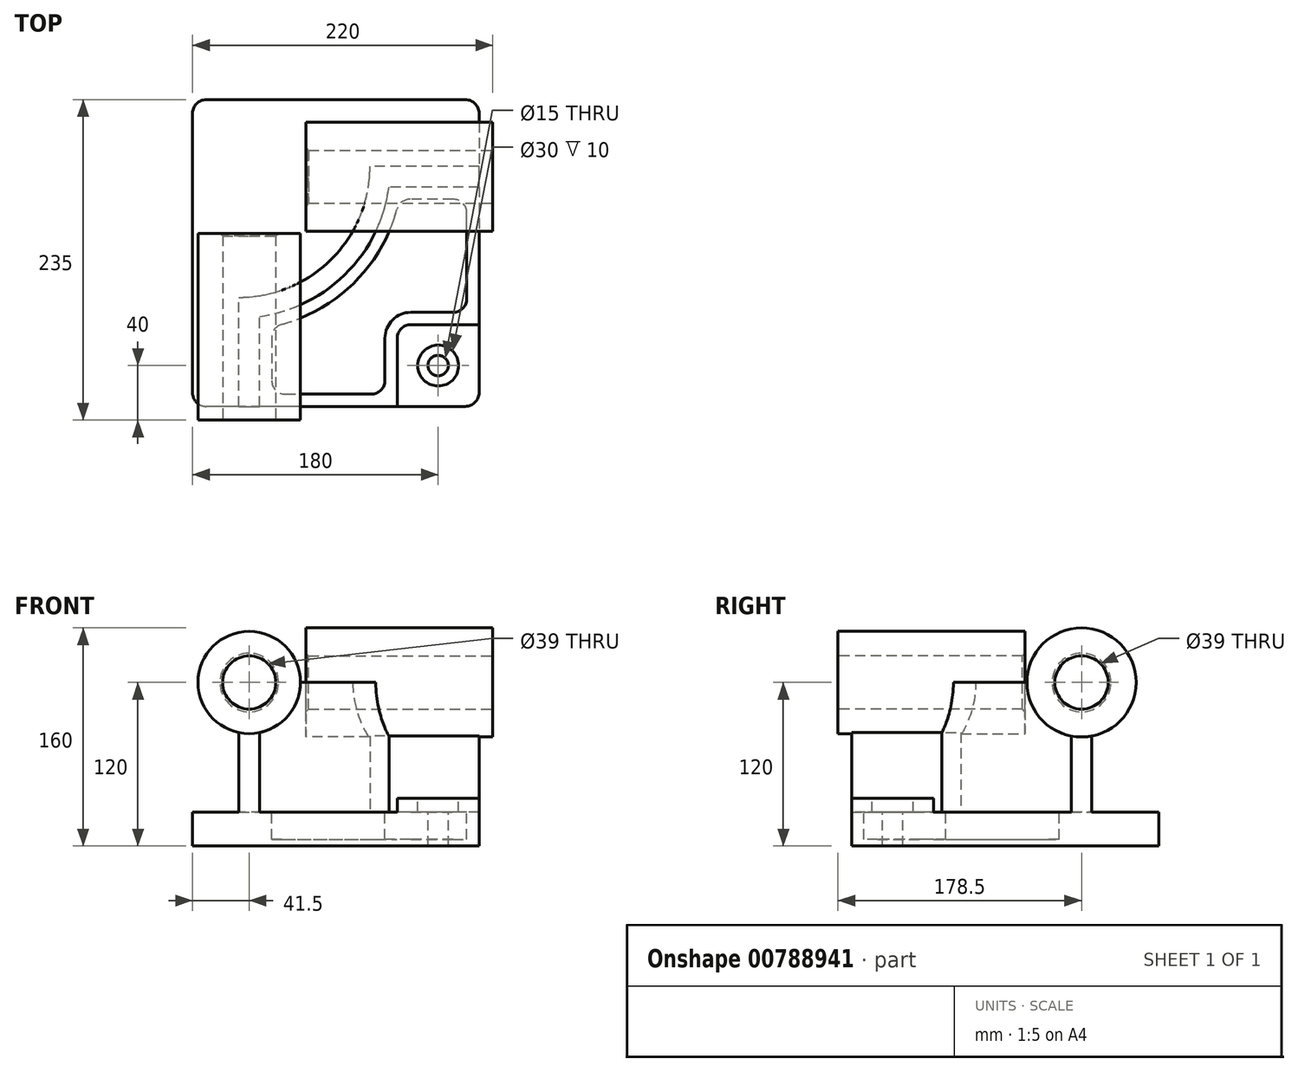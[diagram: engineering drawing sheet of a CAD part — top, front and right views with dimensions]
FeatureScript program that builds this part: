
annotation { "Feature Type Name" : "Feature", "Feature Type Description" : "" }
export const myFeature = defineFeature(function(context is Context, id is Id, definition is map)
    precondition{}
    {
        {
            var Q0;
            Q0=qCreatedBy(makeId("Top.planeOp"),FACE);
            var sketch = newSketch(context, id + "F0", { "sketchPlane" : qUnion([Q0])});
            skLineSegment(sketch, "E0.bottom", {"start": v(105, 112.5) * mm, "end": v(-105, 112.5) * mm});
            skLineSegment(sketch, "E0.top", {"start": v(105, -112.5) * mm, "end": v(-105, -112.5) * mm});
            skLineSegment(sketch, "E0.left", {"start": v(105, 112.5) * mm, "end": v(105, -112.5) * mm});
            skLineSegment(sketch, "E0.right", {"start": v(-105, 112.5) * mm, "end": v(-105, -112.5) * mm});
            skPoint(sketch, "E0.middle", {"position": v(0, 0) * mm});
            skSolve(sketch);
        }
        {
            var Q0;
            Q0=makeQuery(id+"F0.imprint","IMPRINT",FACE,{"disambiguationData":[TD([[makeQuery(id+"F0.imprint","IMPRINT",EDGE,{"derivedFrom":sQuery(id+"F0.wireOp",EDGE,"E0.bottom")}),1.0]])]});
            extrude(context, id + "F1", {"entities" : qUnion([Q0]), "depth" : 25 * mm, "offsetDistance" : 25 * mm});
        }
        {
            var Q0;
            Q0=makeQuery(id+"F1.opExtrude","CAP_FACE",FACE,{"disambiguationData":[OSD([sQuery(id+"F0.wireOp",EDGE,"E0.bottom"),sQuery(id+"F0.wireOp",EDGE,"E0.top"),sQuery(id+"F0.wireOp",EDGE,"E0.left"),sQuery(id+"F0.wireOp",EDGE,"E0.right")])],"isStart":false});
            var sketch = newSketch(context, id + "F2", { "sketchPlane" : qUnion([Q0])});
            skLineSegment(sketch, "E1", {"start": v(-71, -112.5) * mm, "end": v(-71, -32.5) * mm});
            skLineSegment(sketch, "E2", {"start": v(105, 63.5) * mm, "end": v(25, 63.5) * mm});
            skArc(sketch, "E3", {"start": v(-71, -32.5) * mm, "mid": v(-3.12, -4.38) * mm, "end": v(25, 63.5) * mm});
            skLineSegment(sketch, "E4", {"start": v(-71, 63.5) * mm, "end": v(-71, -32.5) * mm, "construction": true});
            skLineSegment(sketch, "E5", {"start": v(25, 63.5) * mm, "end": v(-71, 63.5) * mm, "construction": true});
            skLineSegment(sketch, "E6.0", {"start": v(-56, -112.5) * mm, "end": v(-56, -46.48) * mm});
            skArc(sketch, "E6.1", {"start": v(-56, -46.48) * mm, "mid": v(7.49, -14.99) * mm, "end": v(38.98, 48.5) * mm});
            skLineSegment(sketch, "E6.2", {"start": v(105, 48.5) * mm, "end": v(38.98, 48.5) * mm});
            skLineSegment(sketch, "E7.0", {"start": v(105, 112.5) * mm, "end": v(105, -112.5) * mm});
            skLineSegment(sketch, "E8.0.0", {"start": v(-105, -112.5) * mm, "end": v(105, -112.5) * mm});
            skLineSegment(sketch, "E8.0.1", {"start": v(105, -112.5) * mm, "end": v(105, 112.5) * mm});
            skLineSegment(sketch, "E8.0.2", {"start": v(105, 112.5) * mm, "end": v(-105, 112.5) * mm});
            skLineSegment(sketch, "E8.0.3", {"start": v(-105, 112.5) * mm, "end": v(-105, -112.5) * mm});
            skSolve(sketch);
        }
        {
            var Q0;
            {var subQ2=sQuery(id+"F2.wireOp",EDGE,"E1");Q0=makeQuery(id+"F2.imprint","IMPRINT",FACE,{"disambiguationData":[TD([[makeQuery(id+"F2.imprint","IMPRINT",EDGE,{"derivedFrom":subQ2}),-1.0]])]});}
            extrude(context, id + "F3", {"entities" : qUnion([Q0]), "operationType" : NewBodyOperationType.ADD, "depth" : 95 * mm, "offsetDistance" : 25 * mm});
        }
        {
            var Q0;
            Q0=makeQuery(id+"F3.boolean.opBoolean","MERGE",FACE,{"derivedFrom":[makeQuery(id+"F1.opExtrude","SWEPT_FACE",FACE,{"disambiguationData":[OSD([sQuery(id+"F0.wireOp",EDGE,"E0.top")])]}),makeQuery(id+"F3.opExtrude","SWEPT_FACE",FACE,{"disambiguationData":[OSD([sQuery(id+"F2.wireOp",EDGE,"E8.0.0")])]})]});
            var sketch = newSketch(context, id + "F4", { "sketchPlane" : qUnion([Q0])});
            skCircle(sketch, "E9", {"center": v(-63.5, 120) * mm, "radius": 37.5 * mm});
            skSolve(sketch);
        }
        {
            var Q0;
            Q0 = qSketchRegion(id + "F4", true);
            extrude(context, id + "F5", {"entities" : qUnion([Q0]), "operationType" : NewBodyOperationType.ADD, "depth" : 10 * mm, "offsetDistance" : 25 * mm, "hasSecondDirection" : true, "secondDirectionOppositeDirection" : true, "secondDirectionDepth" : 127 * mm});
        }
        {
            var Q0;
            Q0=makeQuery(id+"F3.boolean.opBoolean","MERGE",FACE,{"derivedFrom":[makeQuery(id+"F1.opExtrude","SWEPT_FACE",FACE,{"disambiguationData":[OSD([sQuery(id+"F0.wireOp",EDGE,"E0.left")])]}),makeQuery(id+"F3.opExtrude","SWEPT_FACE",FACE,{"disambiguationData":[OSD([sQuery(id+"F2.wireOp",EDGE,"E8.0.1")])]})]});
            var sketch = newSketch(context, id + "F6", { "sketchPlane" : qUnion([Q0])});
            skCircle(sketch, "E10", {"center": v(56, 120) * mm, "radius": 40 * mm});
            skSolve(sketch);
        }
        {
            var Q0;
            Q0 = qSketchRegion(id + "F6", true);
            extrude(context, id + "F7", {"entities" : qUnion([Q0]), "operationType" : NewBodyOperationType.ADD, "depth" : 10 * mm, "offsetDistance" : 25 * mm, "hasSecondDirection" : true, "secondDirectionOppositeDirection" : true, "secondDirectionDepth" : 127 * mm});
        }
        {
            var Q0;
            {var subQ0=sQuery(id+"F0.wireOp",EDGE,"E0.left");var subQ1=sQuery(id+"F0.wireOp",EDGE,"E0.top");Q0=makeQuery(id+"F3.boolean.opBoolean","SPLIT",FACE,{"disambiguationData":[TD([makeQuery(id+"F3.opExtrude","SWEPT_FACE",FACE,{"disambiguationData":[OSD([sQuery(id+"F2.wireOp",EDGE,"E6.0")])]})])],"derivedFrom":makeQuery(id+"F1.opExtrude","CAP_FACE",FACE,{"disambiguationData":[OSD([sQuery(id+"F0.wireOp",EDGE,"E0.bottom"),subQ1,subQ0,sQuery(id+"F0.wireOp",EDGE,"E0.right")])],"isStart":false})});}
            var sketch = newSketch(context, id + "F8", { "sketchPlane" : qUnion([Q0])});
            skLineSegment(sketch, "E11.bottom", {"start": v(105, -112.5) * mm, "end": v(45, -112.5) * mm});
            skLineSegment(sketch, "E11.top", {"start": v(105, -52.5) * mm, "end": v(45, -52.5) * mm});
            skLineSegment(sketch, "E11.left", {"start": v(105, -112.5) * mm, "end": v(105, -52.5) * mm});
            skLineSegment(sketch, "E11.right", {"start": v(45, -112.5) * mm, "end": v(45, -52.5) * mm});
            skSolve(sketch);
        }
        {
            var Q0;
            Q0 = qSketchRegion(id + "F8", true);
            extrude(context, id + "F9", {"entities" : qUnion([Q0]), "operationType" : NewBodyOperationType.ADD, "depth" : 10 * mm, "offsetDistance" : 25 * mm});
        }
        {
            var Q0;
            Q0=makeQuery(id+"F9.opExtrude","SWEPT_EDGE",EDGE,{"disambiguationData":[OSD([sQuery(id+"F8.wireOp",EDGE,"E11.top"),sQuery(id+"F8.wireOp",EDGE,"E11.right")])]});
            fillet(context, id + "F10", {"entities" : qUnion([Q0]), "radius" : 10 * mm, "tangentPropagation" : true, "allowEdgeOverflow" : false});
        }
        {
            var Q0;
            {var subQ0=sQuery(id+"F0.wireOp",EDGE,"E0.left");var subQ1=sQuery(id+"F0.wireOp",EDGE,"E0.top");Q0=makeQuery(id+"F3.boolean.opBoolean","SPLIT",FACE,{"disambiguationData":[TD([makeQuery(id+"F3.opExtrude","SWEPT_FACE",FACE,{"disambiguationData":[OSD([sQuery(id+"F2.wireOp",EDGE,"E6.0")])]})])],"derivedFrom":makeQuery(id+"F1.opExtrude","CAP_FACE",FACE,{"disambiguationData":[OSD([sQuery(id+"F0.wireOp",EDGE,"E0.bottom"),subQ1,subQ0,sQuery(id+"F0.wireOp",EDGE,"E0.right")])],"isStart":false})});}
            var sketch = newSketch(context, id + "F11", { "sketchPlane" : qUnion([Q0])});
            skLineSegment(sketch, "E12.0", {"start": v(-47, -54.08) * mm, "end": v(-47, -103.5) * mm});
            skArc(sketch, "E12.1", {"start": v(46.58, 39.5) * mm, "mid": v(13.85, -21.35) * mm, "end": v(-47, -54.08) * mm});
            skLineSegment(sketch, "E12.2", {"start": v(-47, -103.5) * mm, "end": v(36, -103.5) * mm});
            skLineSegment(sketch, "E12.3", {"start": v(96, 39.5) * mm, "end": v(46.58, 39.5) * mm});
            skLineSegment(sketch, "E12.4", {"start": v(36, -103.5) * mm, "end": v(36, -62.5) * mm});
            skArc(sketch, "E12.5", {"start": v(36, -62.5) * mm, "mid": v(41.56, -49.06) * mm, "end": v(55, -43.5) * mm});
            skLineSegment(sketch, "E12.6", {"start": v(55, -43.5) * mm, "end": v(96, -43.5) * mm});
            skLineSegment(sketch, "E12.7", {"start": v(96, -43.5) * mm, "end": v(96, 39.5) * mm});
            skSolve(sketch);
        }
        {
            var Q0;
            Q0=makeQuery(id+"F11.imprint","IMPRINT",FACE,{"disambiguationData":[TD([[makeQuery(id+"F11.imprint","IMPRINT",EDGE,{"derivedFrom":sQuery(id+"F11.wireOp",EDGE,"E12.0")}),1.0]])]});
            extrude(context, id + "F12", {"entities" : qUnion([Q0]), "operationType" : NewBodyOperationType.REMOVE, "oppositeDirection" : true, "depth" : 20 * mm, "offsetDistance" : 25 * mm});
        }
        {
            var Q0;
            Q0=makeQuery(id+"F9.opExtrude","CAP_FACE",FACE,{"disambiguationData":[OSD([sQuery(id+"F8.wireOp",EDGE,"E11.bottom"),sQuery(id+"F8.wireOp",EDGE,"E11.top"),sQuery(id+"F8.wireOp",EDGE,"E11.left"),sQuery(id+"F8.wireOp",EDGE,"E11.right")])],"isStart":false});
            var sketch = newSketch(context, id + "F13", { "sketchPlane" : qUnion([Q0])});
            skCircle(sketch, "E13", {"center": v(75, -82.5) * mm, "radius": 15 * mm});
            skSolve(sketch);
        }
        {
            var Q0;
            Q0=sQuery(id+"F13.wireOp",VERTEX,"E13.center");
            var Q1;
            Q1=makeQuery(id+"F1.opExtrude","SWEPT_BODY",BODY,{"disambiguationData":[OSD([sQuery(id+"F0.wireOp",EDGE,"E0.bottom"),sQuery(id+"F0.wireOp",EDGE,"E0.top"),sQuery(id+"F0.wireOp",EDGE,"E0.left"),sQuery(id+"F0.wireOp",EDGE,"E0.right")])]});
            hole(context, id + "F14", {"style" : HoleStyle.C_BORE, "endStyle" : HoleEndStyle.THROUGH, "holeDiameter" : 15 * mm, "cBoreDiameter" : 30 * mm, "cBoreDepth" : 10 * mm, "majorDiameter" : 6.35 * mm, "isTappedThrough" : true, "tappedDepth" : 12 * mm, "tapClearance" : 3, "locations" : qUnion([Q0]), "scope" : qUnion([Q1])});
        }
        {
            var Q0;
            Q0=makeQuery(id+"F12.boolean.opBoolean","COPY",EDGE,{"derivedFrom":makeQuery(id+"F12.opExtrude","SWEPT_EDGE",EDGE,{"disambiguationData":[OSD([sQuery(id+"F11.wireOp",EDGE,"E12.0"),sQuery(id+"F11.wireOp",EDGE,"E12.1")])]})});
            var Q1;
            Q1=makeQuery(id+"F12.boolean.opBoolean","COPY",EDGE,{"derivedFrom":makeQuery(id+"F12.opExtrude","SWEPT_EDGE",EDGE,{"disambiguationData":[OSD([sQuery(id+"F11.wireOp",EDGE,"E12.1"),sQuery(id+"F11.wireOp",EDGE,"E12.3")])]})});
            var Q2;
            Q2=makeQuery(id+"F12.boolean.opBoolean","COPY",EDGE,{"derivedFrom":makeQuery(id+"F12.opExtrude","SWEPT_EDGE",EDGE,{"disambiguationData":[OSD([sQuery(id+"F11.wireOp",EDGE,"E12.2"),sQuery(id+"F11.wireOp",EDGE,"E12.4")])]})});
            var Q3;
            Q3=makeQuery(id+"F12.boolean.opBoolean","COPY",EDGE,{"derivedFrom":makeQuery(id+"F12.opExtrude","SWEPT_EDGE",EDGE,{"disambiguationData":[OSD([sQuery(id+"F11.wireOp",EDGE,"E12.6"),sQuery(id+"F11.wireOp",EDGE,"E12.7")])]})});
            var Q4;
            Q4=makeQuery(id+"F12.boolean.opBoolean","COPY",EDGE,{"derivedFrom":makeQuery(id+"F12.opExtrude","SWEPT_EDGE",EDGE,{"disambiguationData":[OSD([sQuery(id+"F11.wireOp",EDGE,"E12.3"),sQuery(id+"F11.wireOp",EDGE,"E12.7")])]})});
            var Q5;
            Q5=makeQuery(id+"F12.boolean.opBoolean","COPY",EDGE,{"derivedFrom":makeQuery(id+"F12.opExtrude","SWEPT_EDGE",EDGE,{"disambiguationData":[OSD([sQuery(id+"F11.wireOp",EDGE,"E12.0"),sQuery(id+"F11.wireOp",EDGE,"E12.2")])]})});
            fillet(context, id + "F15", {"entities" : qUnion([Q0, Q1, Q2, Q3, Q4, Q5]), "radius" : 10 * mm, "tangentPropagation" : true, "allowEdgeOverflow" : false});
        }
        {
            var Q0;
            Q0=makeQuery(id+"F5.opExtrude","CAP_FACE",FACE,{"disambiguationData":[OSD([sQuery(id+"F4.wireOp",EDGE,"E9")])],"isStart":false});
            var sketch = newSketch(context, id + "F16", { "sketchPlane" : qUnion([Q0])});
            skCircle(sketch, "E14", {"center": v(-63.5, 120) * mm, "radius": 19.5 * mm});
            skSolve(sketch);
        }
        {
            var Q0;
            Q0 = qSketchRegion(id + "F16", true);
            extrude(context, id + "F17", {"entities" : qUnion([Q0]), "operationType" : NewBodyOperationType.REMOVE, "endBound" : BoundingType.THROUGH_ALL, "oppositeDirection" : true, "depth" : 25 * mm, "offsetDistance" : 25 * mm});
        }
        {
            var Q0;
            Q0=makeQuery(id+"F7.opExtrude","CAP_FACE",FACE,{"disambiguationData":[OSD([sQuery(id+"F6.wireOp",EDGE,"E10")])],"isStart":false});
            var sketch = newSketch(context, id + "F18", { "sketchPlane" : qUnion([Q0])});
            skCircle(sketch, "E15", {"center": v(56, 120) * mm, "radius": 19.5 * mm});
            skSolve(sketch);
        }
        {
            var Q0;
            Q0=makeQuery(id+"F18.imprint","IMPRINT",FACE,{"disambiguationData":[TD([[makeQuery(id+"F18.imprint","IMPRINT",EDGE,{"derivedFrom":sQuery(id+"F18.wireOp",EDGE,"E15")}),1.0]])]});
            extrude(context, id + "F19", {"entities" : qUnion([Q0]), "operationType" : NewBodyOperationType.REMOVE, "endBound" : BoundingType.THROUGH_ALL, "oppositeDirection" : true, "depth" : 25 * mm, "offsetDistance" : 25 * mm});
        }
        {
            var Q0;
            Q0=makeQuery(id+"F17.boolean.opBoolean","COPY",EDGE,{"derivedFrom":makeQuery(id+"F17.opExtrude","CAP_EDGE",EDGE,{"disambiguationData":[OSD([sQuery(id+"F16.wireOp",EDGE,"E14")])],"isStart":true})});
            var Q1;
            Q1=makeQuery(id+"F19.boolean.opBoolean","COPY",EDGE,{"derivedFrom":makeQuery(id+"F19.opExtrude","CAP_EDGE",EDGE,{"disambiguationData":[OSD([sQuery(id+"F18.wireOp",EDGE,"E15")])],"isStart":true})});
            var Q2;
            Q2=makeQuery(id+"F17.boolean.opBoolean","INTERSECT",EDGE,{"derivedFrom":[makeQuery(id+"F5.opExtrude","CAP_FACE",FACE,{"disambiguationData":[OSD([sQuery(id+"F4.wireOp",EDGE,"E9")])],"isStart":true}),makeQuery(id+"F17.opExtrude","SWEPT_FACE",FACE,{"disambiguationData":[OSD([sQuery(id+"F16.wireOp",EDGE,"E14")])]})]});
            var Q3;
            Q3=makeQuery(id+"F19.boolean.opBoolean","INTERSECT",EDGE,{"derivedFrom":[makeQuery(id+"F7.opExtrude","CAP_FACE",FACE,{"disambiguationData":[OSD([sQuery(id+"F6.wireOp",EDGE,"E10")])],"isStart":true}),makeQuery(id+"F19.opExtrude","SWEPT_FACE",FACE,{"disambiguationData":[OSD([sQuery(id+"F18.wireOp",EDGE,"E15")])]})]});
            chamfer(context, id + "F20", {"entities" : qUnion([Q0, Q1, Q2, Q3]), "width" : 2 * mm, "tangentPropagation" : true});
        }
        {
            var Q0;
            Q0=makeQuery(id+"F1.opExtrude","SWEPT_EDGE",EDGE,{"disambiguationData":[OSD([sQuery(id+"F0.wireOp",EDGE,"E0.bottom"),sQuery(id+"F0.wireOp",EDGE,"E0.right")])]});
            var Q1;
            Q1=makeQuery(id+"F1.opExtrude","SWEPT_EDGE",EDGE,{"disambiguationData":[OSD([sQuery(id+"F0.wireOp",EDGE,"E0.bottom"),sQuery(id+"F0.wireOp",EDGE,"E0.left")])]});
            var Q2;
            Q2=makeQuery(id+"F9.boolean.opBoolean","MERGE",EDGE,{"derivedFrom":[makeQuery(id+"F1.opExtrude","SWEPT_EDGE",EDGE,{"disambiguationData":[OSD([sQuery(id+"F0.wireOp",EDGE,"E0.top"),sQuery(id+"F0.wireOp",EDGE,"E0.left")])]}),makeQuery(id+"F9.opExtrude","SWEPT_EDGE",EDGE,{"disambiguationData":[OSD([sQuery(id+"F8.wireOp",EDGE,"E11.bottom"),sQuery(id+"F8.wireOp",EDGE,"E11.left")])]})]});
            var Q3;
            Q3=makeQuery(id+"F1.opExtrude","SWEPT_EDGE",EDGE,{"disambiguationData":[OSD([sQuery(id+"F0.wireOp",EDGE,"E0.top"),sQuery(id+"F0.wireOp",EDGE,"E0.right")])]});
            fillet(context, id + "F21", {"entities" : qUnion([Q0, Q1, Q2, Q3]), "radius" : 10 * mm, "tangentPropagation" : true, "allowEdgeOverflow" : false});
        }
    });
